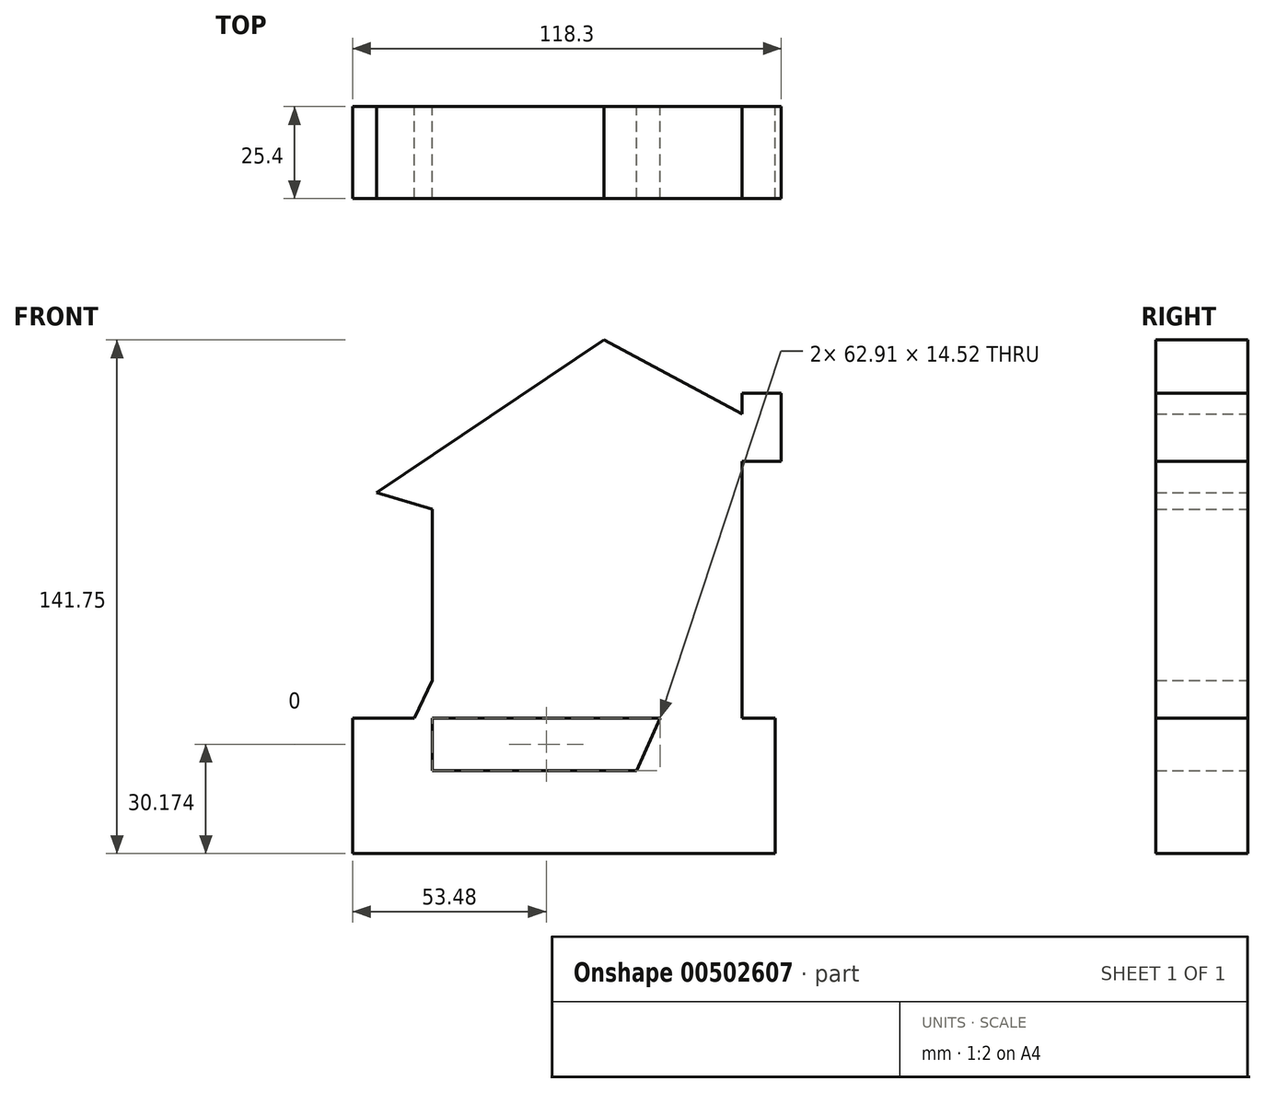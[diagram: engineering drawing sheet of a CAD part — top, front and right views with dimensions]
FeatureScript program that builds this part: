
annotation { "Feature Type Name" : "Feature", "Feature Type Description" : "" }
export const myFeature = defineFeature(function(context is Context, id is Id, definition is map)
    precondition{}
    {
        {
            var Q0;
            Q0=qCreatedBy(makeId("Front.planeOp"),FACE);
            var sketch = newSketch(context, id + "F0", { "sketchPlane" : qUnion([Q0])});
            skLineSegment(sketch, "E0.bottom", {"start": v(-33.95, 53.18) * mm, "end": v(51.54, 53.18) * mm});
            skLineSegment(sketch, "E0.top", {"start": v(-33.95, -32.1) * mm, "end": v(51.54, -32.1) * mm});
            skLineSegment(sketch, "E0.left", {"start": v(-33.95, 53.18) * mm, "end": v(-33.95, -32.1) * mm});
            skLineSegment(sketch, "E0.right", {"start": v(51.54, 53.18) * mm, "end": v(51.54, -32.1) * mm});
            skLineSegment(sketch, "E1.bottom", {"start": v(62.32, 72.06) * mm, "end": v(51.54, 72.06) * mm});
            skLineSegment(sketch, "E1.top", {"start": v(62.32, 53.18) * mm, "end": v(51.54, 53.18) * mm});
            skLineSegment(sketch, "E1.left", {"start": v(62.32, 72.06) * mm, "end": v(62.32, 53.18) * mm});
            skLineSegment(sketch, "E1.right", {"start": v(51.54, 72.06) * mm, "end": v(51.54, 53.18) * mm});
            skLineSegment(sketch, "E2.bottom", {"start": v(60.69, -17.57) * mm, "end": v(-55.98, -17.57) * mm});
            skLineSegment(sketch, "E2.top", {"start": v(60.69, -55) * mm, "end": v(-55.98, -55) * mm});
            skLineSegment(sketch, "E2.left", {"start": v(60.69, -17.57) * mm, "end": v(60.69, -55) * mm});
            skLineSegment(sketch, "E2.right", {"start": v(-55.98, -17.57) * mm, "end": v(-55.98, -55) * mm});
            skLineSegment(sketch, "E3", {"start": v(-13.37, 36.61) * mm, "end": v(-47, -34.92) * mm});
            skLineSegment(sketch, "E4", {"start": v(-47, -34.92) * mm, "end": v(15.76, -46.87) * mm});
            skLineSegment(sketch, "E5", {"start": v(15.76, -46.87) * mm, "end": v(45.77, 19.77) * mm});
            skLineSegment(sketch, "E6", {"start": v(45.77, 19.77) * mm, "end": v(-15.84, 34.7) * mm});
            skLineSegment(sketch, "E7", {"start": v(-15.84, 34.7) * mm, "end": v(-49.38, 44.61) * mm});
            skLineSegment(sketch, "E8", {"start": v(-49.38, 44.61) * mm, "end": v(13.4, 86.74) * mm});
            skLineSegment(sketch, "E9", {"start": v(13.4, 86.74) * mm, "end": v(52.67, 65.71) * mm});
            skLineSegment(sketch, "E10", {"start": v(52.67, 65.71) * mm, "end": v(-8.03, 43.64) * mm});
            skLineSegment(sketch, "E11", {"start": v(-8.03, 43.64) * mm, "end": v(-10.8, 39.32) * mm});
            skSolve(sketch);
        }
        {
            var Q0;
            Q0 = qSketchRegion(id + "F0", true);
            extrude(context, id + "F1", {"entities" : qUnion([Q0]), "depth" : 25.4 * mm, "offsetDistance" : 25.4 * mm});
        }
    });
